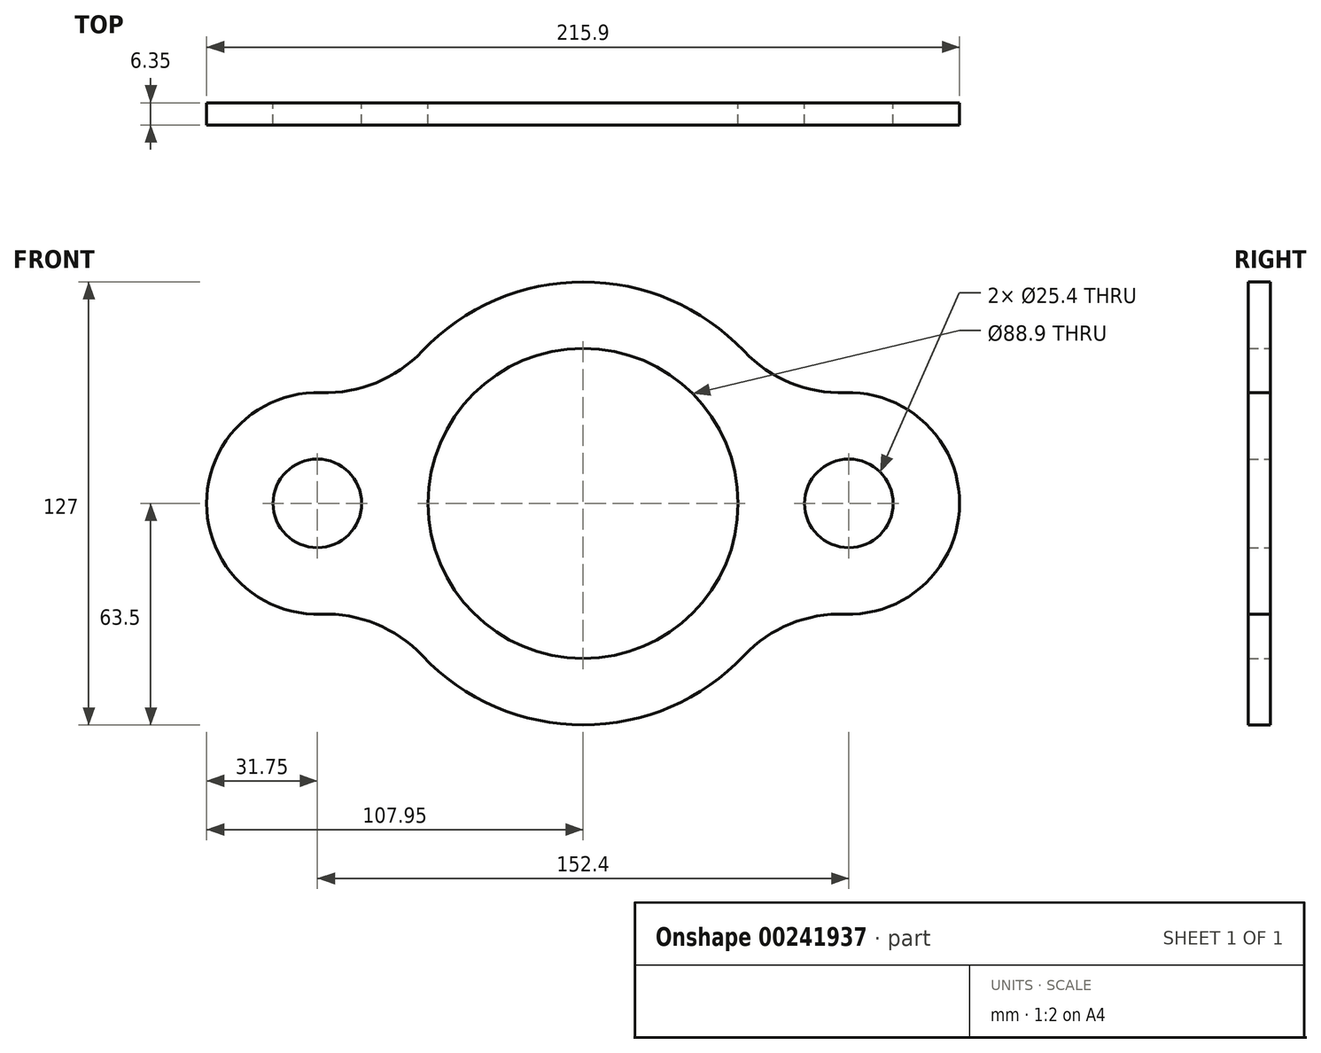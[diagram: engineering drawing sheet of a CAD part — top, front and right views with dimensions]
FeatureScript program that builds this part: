
annotation { "Feature Type Name" : "Feature", "Feature Type Description" : "" }
export const myFeature = defineFeature(function(context is Context, id is Id, definition is map)
    precondition{}
    {
        {
            var Q0;
            Q0=qCreatedBy(makeId("Front.planeOp"),FACE);
            var sketch = newSketch(context, id + "F0", { "sketchPlane" : qUnion([Q0])});
            skCircle(sketch, "E0", {"center": v(0, 0) * mm, "radius": 44.45 * mm});
            skArc(sketch, "E1", {"start": v(-46.14, -43.63) * mm, "mid": v(0, -63.5) * mm, "end": v(46.14, -43.63) * mm});
            skCircle(sketch, "E2", {"center": v(76.2, 0) * mm, "radius": 12.7 * mm});
            skArc(sketch, "E3", {"start": v(75.12, -31.73) * mm, "mid": v(107.95, 0) * mm, "end": v(75.12, 31.73) * mm});
            skCircle(sketch, "E4", {"center": v(-76.2, 0) * mm, "radius": 12.7 * mm});
            skArc(sketch, "E5", {"start": v(-75.12, 31.73) * mm, "mid": v(-107.95, 0) * mm, "end": v(-75.12, -31.73) * mm});
            skArc(sketch, "E6.trimOffspring", {"start": v(46.14, 43.63) * mm, "mid": v(0, 63.5) * mm, "end": v(-46.14, 43.63) * mm});
            skArc(sketch, "E7.filletArc", {"start": v(-75.12, 31.73) * mm, "mid": v(-59.35, 34.56) * mm, "end": v(-46.14, 43.63) * mm});
            skArc(sketch, "E8.filletArc", {"start": v(46.14, 43.63) * mm, "mid": v(59.35, 34.56) * mm, "end": v(75.12, 31.73) * mm});
            skArc(sketch, "E9.filletArc", {"start": v(75.12, -31.73) * mm, "mid": v(59.35, -34.56) * mm, "end": v(46.14, -43.63) * mm});
            skArc(sketch, "E10.filletArc", {"start": v(-46.14, -43.63) * mm, "mid": v(-59.35, -34.56) * mm, "end": v(-75.12, -31.73) * mm});
            skSolve(sketch);
        }
        {
            var Q0;
            Q0=makeQuery(id+"F0.imprint","IMPRINT",FACE,{"disambiguationData":[TD([[makeQuery(id+"F0.imprint","IMPRINT",EDGE,{"derivedFrom":sQuery(id+"F0.wireOp",EDGE,"E0")}),-1.0]])]});
            extrude(context, id + "F1", {"entities" : qUnion([Q0]), "depth" : 6.35 * mm});
        }
    });
